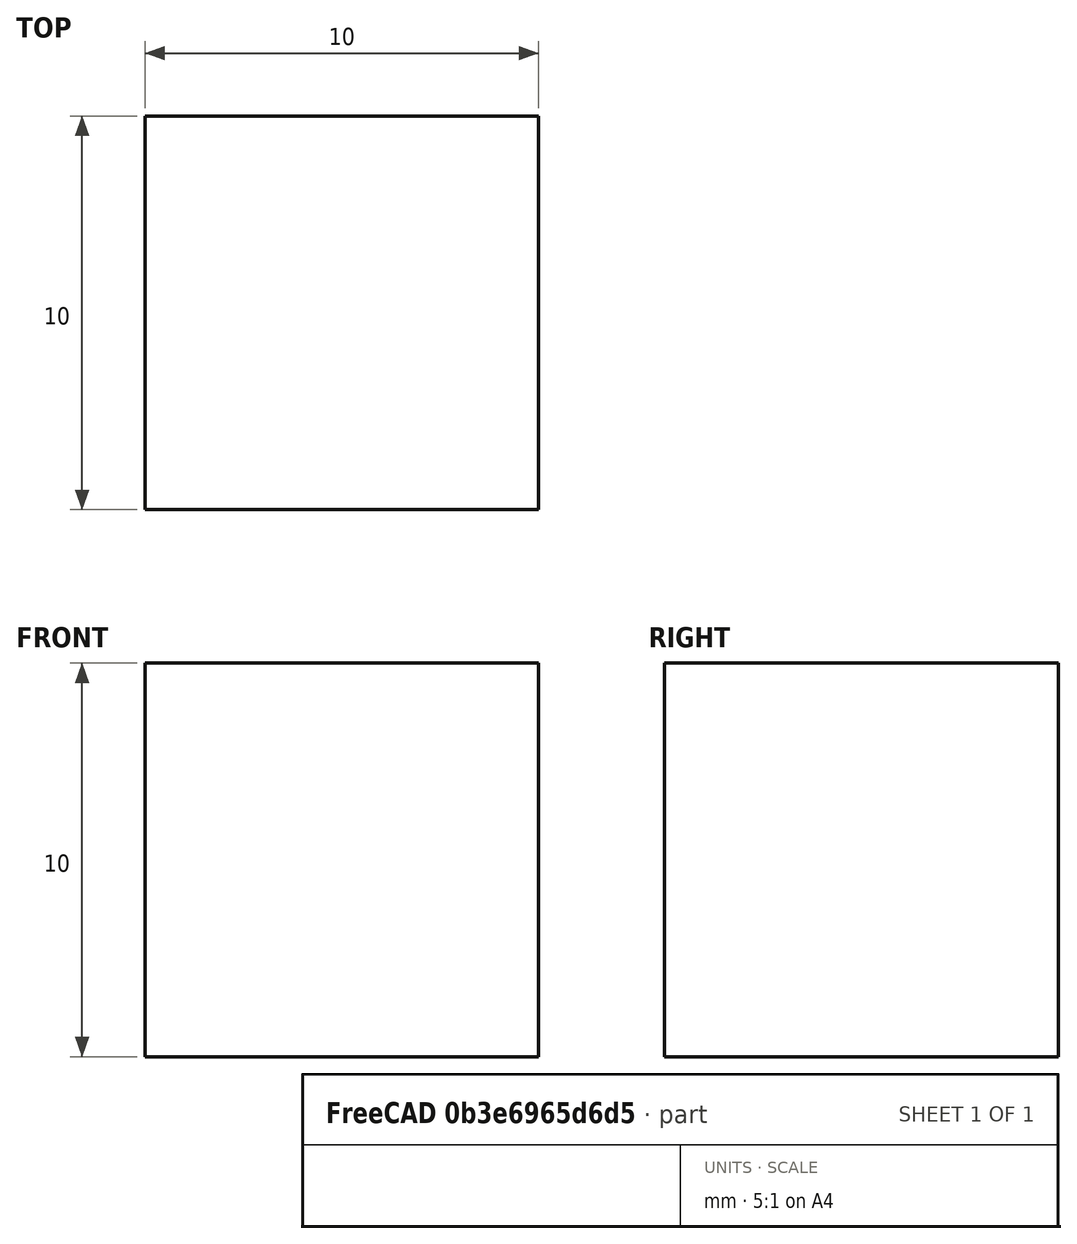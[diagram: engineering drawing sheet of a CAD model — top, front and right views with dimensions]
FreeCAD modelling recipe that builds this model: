
FCSTD DOCUMENT  (FreeCAD 0.21R33694 (Git))
Label: Simple Shear
License: All rights reserved
LicenseURL: http://en.wikipedia.org/wiki/All_rights_reserved
objects: Fem::ConstraintForce×4, Fem::ConstraintDisplacement×2, Part::Box×1, Fem::FemSolverObjectPython×1, App::MaterialObjectPython×1, Fem::FemMeshObjectPython×1, Fem::ConstraintFixed×1, Fem::FemAnalysis×1
note: 1 computed .brp shape members not serialized (recipe doc carries the construction recipe); baked Part::Feature solids carry a one-line shape summary decoded from their .brp

FEATURE [Part::Box] Box  label="Cube"
  AttacherType = Attacher::AttachEngine3D
  Height = 10
  Length = 10
  Width = 10
FEATURE [Fem::FemSolverObjectPython] SolverCcxTools  # FEM object (typed FeaturePython)
  AnalysisType = 0
  BeamShellResultOutput3D = false
  BucklingFactors = 1
  EigenmodeHighLimit = 1000000
  EigenmodeLowLimit = 0
  EigenmodesCount = 10
  GeometricalNonlinearity = 0
  IterationsControlParameterCutb = 0.25,0.5,0.75,0.85,,,1.5,
  IterationsControlParameterIter = 4,8,9,200,10,400,,200,,
  IterationsControlParameterTimeUse = false
  IterationsThermoMechMaximum = 2000
  IterationsUserDefinedIncrementations = false
  IterationsUserDefinedTimeStepLength = false
  MaterialNonlinearity = 0
  MatrixSolverType = 0
  SplitInputWriter = false
  ThermoMechSteadyState = true
  TimeEnd = 1
  TimeInitialStep = 0.01
FEATURE [App::MaterialObjectPython] MaterialSolid  # material (typed FeaturePython)
  Category = 0
  Material = AuthorAndLicense=(c) 2013 Juergen Riegel (CC-BY 3.0),CardName=Steel-Generic,Density=7900 kg/m^3,+9 more (map truncated)
FEATURE [Fem::FemMeshObjectPython] FEMMeshGmsh  # FEM object (typed FeaturePython)
  Algorithm2D = 0
  Algorithm3D = 0
  CharacteristicLengthMax = 0
  CharacteristicLengthMin = 10
  CoherenceMesh = true
  ElementDimension = 0
  ElementOrder = 1
  GeometryTolerance = 1e-06
  GroupsOfNodes = false
  HighOrderOptimize = 0
  MeshSizeFromCurvature = 12
  OptimizeNetgen = false
  OptimizeStd = true
  Part = -> Box
  RecombinationAlgorithm = 0
  Recombine3DAll = false
  RecombineAll = false
  SecondOrderLinear = false
FEATURE [Fem::ConstraintForce] ConstraintForce
  Direction = -> Box [Edge10]
  DirectionVector = (1,0,0)
  Force = 10000
  NormalDirection = (0,0,1)
  Points = (9) [(0,0,10),(5,0,10),(10,0,10),(0,5,10),(5,5,10),(10,5,10),(0,10,10),(5,10,10),(10,10,10)]
  References = -> [Box]
FEATURE [Fem::ConstraintForce] ConstraintForce001
  Direction = -> Box [Edge5]
  DirectionVector = (0,0,1)
  Force = 10000
  NormalDirection = (1,0,0)
  Points = (9) [(10,10,0),(10,10,5),(10,10,10),(10,5,0),(10,5,5),(10,5,10),(10,0,0),(10,0,5),(10,0,10)]
  References = -> [Box]
FEATURE [Fem::ConstraintForce] ConstraintForce002
  Direction = -> Box [Edge1]
  DirectionVector = (0,0,-1)
  Force = 10000
  NormalDirection = (-1,0,0)
  Points = (9) [(0,10,0),(0,10,5),(0,10,10),(0,5,0),(0,5,5),(0,5,10),(0,0,0),(0,0,5),(0,0,10)]
  References = -> [Box]
  Reversed = true
FEATURE [Fem::ConstraintForce] ConstraintForce003
  Direction = -> Box [Edge9]
  DirectionVector = (-1,0,0)
  Force = 10000
  NormalDirection = (0,0,-1)
  Points = (9) [(0,0,0),(5,0,0),(10,0,0),(0,5,0),(5,5,0),(10,5,0),(0,10,0),(5,10,0),(10,10,0)]
  References = -> [Box]
  Reversed = true
FEATURE [Fem::ConstraintFixed] ConstraintFixed
  NormalDirection = (0,0,1)
  Normals = (1) [(0,0,1)]
  Points = (1) [(0,0,0)]
  References = -> [Box]
  Scale = 2
FEATURE [Fem::ConstraintDisplacement] ConstraintDisplacement
  NormalDirection = (0,0,1)
  Normals = (1) [(0,0,1)]
  Points = (1) [(0,10,0)]
  References = -> [Box]
  Scale = 2
  hasXFormula = false
  hasYFormula = false
  hasZFormula = false
  rotxFix = false
  rotxFree = true
  rotyFix = false
  rotyFree = true
  rotzFix = false
  rotzFree = true
  useFlowSurfaceForce = false
  xDisplacement = 0
  xFix = false
  xFree = false
  xRotation = 0
  yDisplacement = 0
  yFix = false
  yFree = true
  yRotation = 0
  zDisplacement = 0
  zFix = false
  zFree = false
  zRotation = 0
FEATURE [Fem::ConstraintDisplacement] ConstraintDisplacement001
  NormalDirection = (0,0,1)
  Normals = (1) [(0,0,1)]
  Points = (1) [(10,0,0)]
  References = -> [Box]
  Scale = 2
  hasXFormula = false
  hasYFormula = false
  hasZFormula = false
  rotxFix = false
  rotxFree = true
  rotyFix = false
  rotyFree = true
  rotzFix = false
  rotzFree = true
  useFlowSurfaceForce = false
  xDisplacement = 0
  xFix = false
  xFree = true
  xRotation = 0
  yDisplacement = 0
  yFix = false
  yFree = true
  yRotation = 0
  zDisplacement = 0
  zFix = false
  zFree = false
  zRotation = 0
FEATURE [Fem::FemAnalysis] Analysis
  Group = -> [SolverCcxTools,MaterialSolid,FEMMeshGmsh,ConstraintForce,ConstraintForce001,ConstraintForce002,ConstraintForce003,ConstraintFixed,ConstraintDisplacement,ConstraintDisplacement001]
